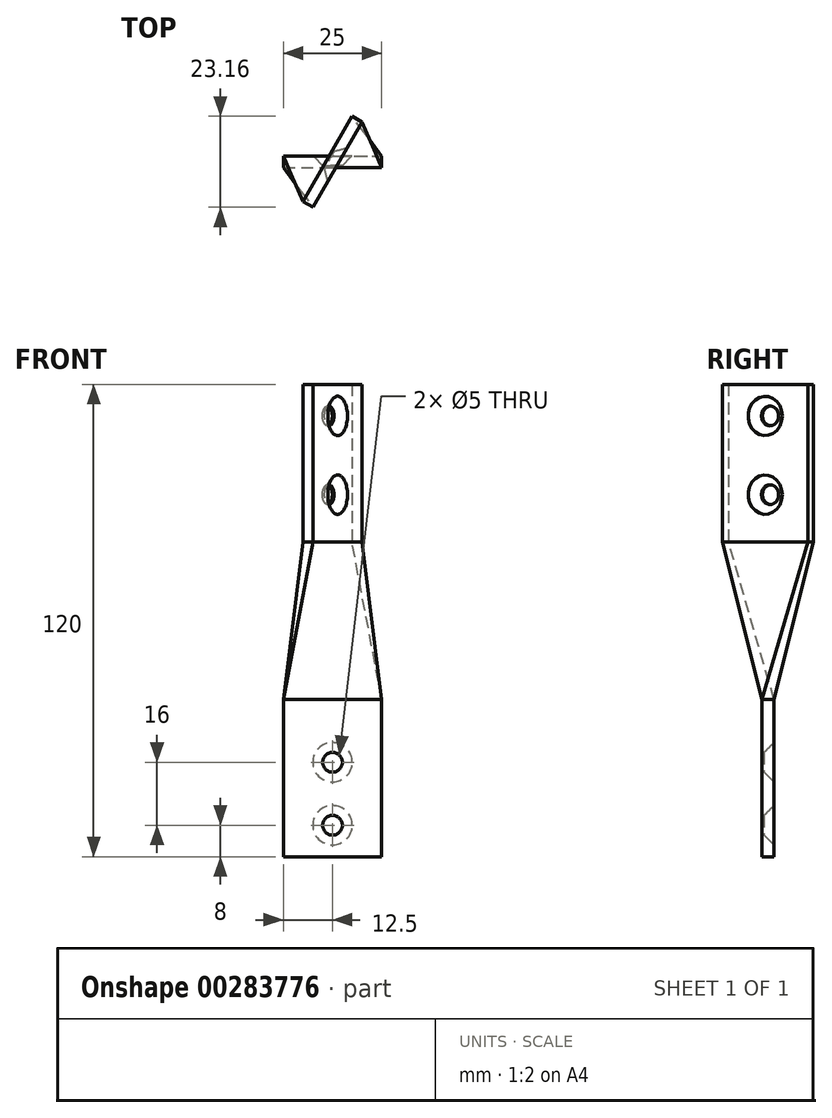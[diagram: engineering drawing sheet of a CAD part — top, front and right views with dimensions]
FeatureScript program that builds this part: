
annotation { "Feature Type Name" : "Feature", "Feature Type Description" : "" }
export const myFeature = defineFeature(function(context is Context, id is Id, definition is map)
    precondition{}
    {
        {
            var Q0;
            Q0=qCreatedBy(makeId("Front.planeOp"),FACE);
            var sketch = newSketch(context, id + "F0", { "sketchPlane" : qUnion([Q0])});
            skLineSegment(sketch, "E0.bottom", {"start": v(-12.5, 0) * mm, "end": v(12.5, 0) * mm});
            skLineSegment(sketch, "E0.top", {"start": v(-12.5, -40) * mm, "end": v(12.5, -40) * mm});
            skLineSegment(sketch, "E0.left", {"start": v(-12.5, 0) * mm, "end": v(-12.5, -40) * mm});
            skLineSegment(sketch, "E0.right", {"start": v(12.5, 0) * mm, "end": v(12.5, -40) * mm});
            skSolve(sketch);
        }
        {
            var Q0;
            Q0=makeQuery(id+"F0.imprint","IMPRINT",FACE,{"disambiguationData":[TD([[makeQuery(id+"F0.imprint","IMPRINT",EDGE,{"derivedFrom":sQuery(id+"F0.wireOp",EDGE,"E0.bottom")}),-1.0]])]});
            extrude(context, id + "F1", {"entities" : qUnion([Q0]), "endBound" : BoundingType.SYMMETRIC, "depth" : 3 * mm});
        }
        {
            var Q0;
            Q0=qCreatedBy(makeId("Front.planeOp"),FACE);
            var sketch = newSketch(context, id + "F2", { "sketchPlane" : qUnion([Q0])});
            skLineSegment(sketch, "E1", {"start": v(0, 60.82) * mm, "end": v(0, -56.5) * mm, "construction": true});
            skSolve(sketch);
        }
        {
            var Q0;
            Q0=sQuery(id+"F2.wireOp",EDGE,"E1");
            cPlane(context, id + "F3", {"entities" : qUnion([Q0]), "cplaneType" : CPlaneType.LINE_ANGLE, "offset" : 25 * mm, "angle" : 30 * degree, "width" : 150 * mm, "height" : 150 * mm});
        }
        {
            var Q0;
            Q0=qCreatedBy(id+"F3.planeOp",FACE);
            var sketch = newSketch(context, id + "F4", { "sketchPlane" : qUnion([Q0])});
            skLineSegment(sketch, "E2.bottom", {"start": v(12.5, 80) * mm, "end": v(-12.5, 80) * mm});
            skLineSegment(sketch, "E2.top", {"start": v(12.5, 40) * mm, "end": v(-12.5, 40) * mm});
            skLineSegment(sketch, "E2.left", {"start": v(12.5, 80) * mm, "end": v(12.5, 40) * mm});
            skLineSegment(sketch, "E2.right", {"start": v(-12.5, 80) * mm, "end": v(-12.5, 40) * mm});
            skSolve(sketch);
        }
        {
            var Q0;
            Q0=makeQuery(id+"F4.imprint","IMPRINT",FACE,{"disambiguationData":[TD([[makeQuery(id+"F4.imprint","IMPRINT",EDGE,{"derivedFrom":sQuery(id+"F4.wireOp",EDGE,"E2.bottom")}),1.0]])]});
            extrude(context, id + "F5", {"entities" : qUnion([Q0]), "endBound" : BoundingType.SYMMETRIC, "depth" : 3 * mm});
        }
        {
            var Q2;
            Q2=makeQuery(id+"F1.opExtrude","SWEPT_FACE",FACE,{"disambiguationData":[OSD([sQuery(id+"F0.wireOp",EDGE,"E0.bottom")])]});
            var Q3;
            Q3=makeQuery(id+"F5.opExtrude","SWEPT_FACE",FACE,{"disambiguationData":[OSD([sQuery(id+"F4.wireOp",EDGE,"E2.top")])]});
            loft(context, id + "F6", {"operationType" : NewBodyOperationType.ADD, "sheetProfilesArray" : [{ "sheetProfileEntities" : qUnion([Q2]) }, { "sheetProfileEntities" : qUnion([Q3]) }]});
        }
        {
            var Q0;
            Q0=makeQuery(id+"F1.opExtrude","CAP_FACE",FACE,{"disambiguationData":[OSD([sQuery(id+"F0.wireOp",EDGE,"E0.bottom"),sQuery(id+"F0.wireOp",EDGE,"E0.top"),sQuery(id+"F0.wireOp",EDGE,"E0.left"),sQuery(id+"F0.wireOp",EDGE,"E0.right")])],"isStart":true});
            var sketch = newSketch(context, id + "F7", { "sketchPlane" : qUnion([Q0])});
            skPoint(sketch, "E3", {"position": v(0, -32) * mm});
            skPoint(sketch, "E4", {"position": v(0, -16) * mm});
            skSolve(sketch);
        }
        {
            var Q0;
            Q0=sQuery(id+"F7.wireOp",VERTEX,"E3");
            var Q1;
            Q1=sQuery(id+"F7.wireOp",VERTEX,"E4");
            var Q2;
            Q2=makeQuery(id+"F1.opExtrude","SWEPT_BODY",BODY,{"disambiguationData":[OSD([sQuery(id+"F0.wireOp",EDGE,"E0.bottom"),sQuery(id+"F0.wireOp",EDGE,"E0.top"),sQuery(id+"F0.wireOp",EDGE,"E0.left"),sQuery(id+"F0.wireOp",EDGE,"E0.right")])]});
            hole(context, id + "F8", {"style" : HoleStyle.C_SINK, "endStyle" : HoleEndStyle.THROUGH, "holeDiameter" : 5 * mm, "cSinkDiameter" : 10 * mm, "cSinkAngle" : 90 * degree, "tappedDepth" : 12 * mm, "tapClearance" : 3, "locations" : qUnion([Q0, Q1]), "scope" : qUnion([Q2])});
        }
        {
            var Q0;
            Q0=makeQuery(id+"F5.opExtrude","CAP_FACE",FACE,{"disambiguationData":[OSD([sQuery(id+"F4.wireOp",EDGE,"E2.bottom"),sQuery(id+"F4.wireOp",EDGE,"E2.top"),sQuery(id+"F4.wireOp",EDGE,"E2.left"),sQuery(id+"F4.wireOp",EDGE,"E2.right")])],"isStart":true});
            var sketch = newSketch(context, id + "F9", { "sketchPlane" : qUnion([Q0])});
            skPoint(sketch, "E5", {"position": v(0, 52) * mm});
            skPoint(sketch, "E6", {"position": v(0, 72) * mm});
            skSolve(sketch);
        }
        {
            var Q0;
            Q0=sQuery(id+"F9.wireOp",VERTEX,"E6");
            var Q1;
            Q1=sQuery(id+"F9.wireOp",VERTEX,"E5");
            var Q2;
            Q2=makeQuery(id+"F1.opExtrude","SWEPT_BODY",BODY,{"disambiguationData":[OSD([sQuery(id+"F0.wireOp",EDGE,"E0.bottom"),sQuery(id+"F0.wireOp",EDGE,"E0.top"),sQuery(id+"F0.wireOp",EDGE,"E0.left"),sQuery(id+"F0.wireOp",EDGE,"E0.right")])]});
            hole(context, id + "F10", {"style" : HoleStyle.C_SINK, "endStyle" : HoleEndStyle.THROUGH, "holeDiameter" : 5 * mm, "cSinkDiameter" : 10 * mm, "cSinkAngle" : 90 * degree, "tappedDepth" : 12 * mm, "tapClearance" : 3, "locations" : qUnion([Q0, Q1]), "scope" : qUnion([Q2])});
        }
    });
